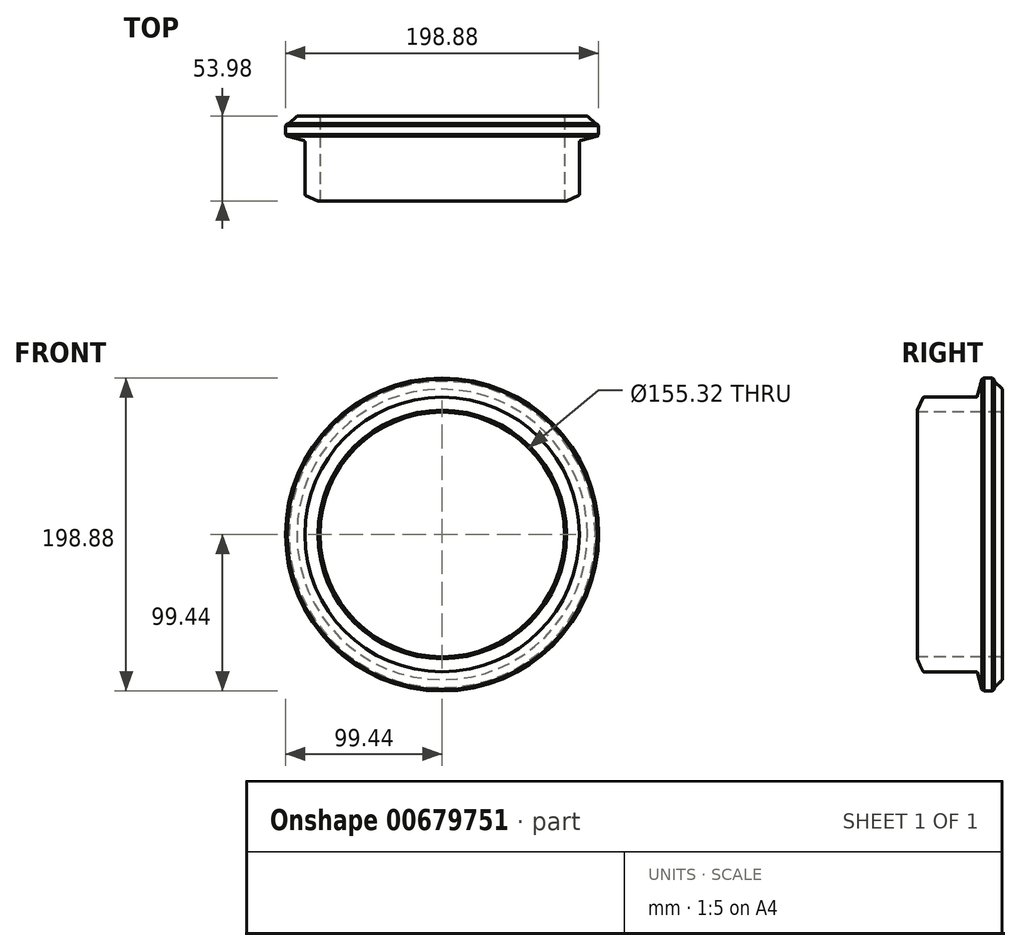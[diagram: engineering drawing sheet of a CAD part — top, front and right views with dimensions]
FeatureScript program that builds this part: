
annotation { "Feature Type Name" : "Feature", "Feature Type Description" : "" }
export const myFeature = defineFeature(function(context is Context, id is Id, definition is map)
    precondition{}
    {
        {
            var Q0;
            Q0=qCreatedBy(makeId("Right.planeOp"),FACE);
            var sketch = newSketch(context, id + "F0", { "sketchPlane" : qUnion([Q0])});
            skPoint(sketch, "E0", {"position": v(0, 77.66) * mm});
            skLineSegment(sketch, "E1", {"start": v(26.99, 77.66) * mm, "end": v(26.99, 92.27) * mm});
            skLineSegment(sketch, "E2", {"start": v(25.8, 93.46) * mm, "end": v(23.09, 96.16) * mm});
            skLineSegment(sketch, "E3", {"start": v(21.96, 97.3) * mm, "end": v(21.96, 99.44) * mm});
            skLineSegment(sketch, "E4", {"start": v(21.96, 99.44) * mm, "end": v(14.27, 99.44) * mm});
            skLineSegment(sketch, "E5", {"start": v(14.27, 99.44) * mm, "end": v(10.99, 87.19) * mm});
            skLineSegment(sketch, "E6", {"start": v(10.99, 87.19) * mm, "end": v(-23.29, 87.19) * mm});
            skLineSegment(sketch, "E7", {"start": v(-23.29, 87.19) * mm, "end": v(-26.99, 78.93) * mm});
            skLineSegment(sketch, "E8", {"start": v(-26.99, 78.42) * mm, "end": v(-26.99, 78.39) * mm});
            skPoint(sketch, "E9.visualSharp", {"position": v(26.99, 77.66) * mm});
            skPoint(sketch, "E10.visualSharp", {"position": v(-26.99, 77.66) * mm});
            skPoint(sketch, "E11.visualSharp", {"position": v(10.99, 87.19) * mm});
            skPoint(sketch, "E12.visualSharp", {"position": v(-26.99, 78.93) * mm});
            skPoint(sketch, "E13.visualSharp", {"position": v(21.96, 97.3) * mm});
            skPoint(sketch, "E14.visualSharp", {"position": v(26.99, 92.27) * mm});
            skLineSegment(sketch, "E15", {"start": v(-61.18, -80.92) * mm, "end": v(40.68, -80.92) * mm, "construction": true});
            skLineSegment(sketch, "E16", {"start": v(21.96, 97.3) * mm, "end": v(26.99, 92.27) * mm});
            skLineSegment(sketch, "E17", {"start": v(26.99, 77.66) * mm, "end": v(-26.99, 77.66) * mm});
            skLineSegment(sketch, "E18", {"start": v(-26.99, 78.93) * mm, "end": v(-26.99, 77.66) * mm});
            skLineSegment(sketch, "E19", {"start": v(-31.2, 0) * mm, "end": v(25.51, 0) * mm, "construction": true});
            skSolve(sketch);
        }
        {
            var Q0;
            {var subQ1=sQuery(id+"F0.wireOp",EDGE,"E1");Q0=makeQuery(id+"F0.imprint","IMPRINT",FACE,{"disambiguationData":[TD([[makeQuery(id+"F0.imprint","IMPRINT",EDGE,{"derivedFrom":subQ1}),1.0]])]});}
            var Q1;
            Q1=sQuery(id+"F0.wireOp",EDGE,"E19");
            revolve(context, id + "F1", {"entities" : qUnion([Q0]), "axis" : qUnion([Q1]), "revolveType" : RevolveType.FULL});
        }
        {
            var Q0;
            Q0=makeQuery(id+"F1.opRevolve","SWEPT_EDGE",EDGE,{"disambiguationData":[OSD([sQuery(id+"F0.wireOp",EDGE,"E5"),sQuery(id+"F0.wireOp",EDGE,"E6")])]});
            var Q1;
            Q1=makeQuery(id+"F1.opRevolve","SWEPT_EDGE",EDGE,{"disambiguationData":[OSD([sQuery(id+"F0.wireOp",EDGE,"E6"),sQuery(id+"F0.wireOp",EDGE,"E7")])]});
            fillet(context, id + "F2", {"entities" : qUnion([Q0, Q1]), "radius" : 0.76 * mm, "tangentPropagation" : true, "allowEdgeOverflow" : false});
        }
        {
            var Q0;
            Q0=makeQuery(id+"F1.opRevolve","SWEPT_EDGE",EDGE,{"disambiguationData":[OSD([sQuery(id+"F0.wireOp",EDGE,"E3"),sQuery(id+"F0.wireOp",EDGE,"E4")])]});
            var Q1;
            Q1=makeQuery(id+"F1.opRevolve","SWEPT_EDGE",EDGE,{"disambiguationData":[OSD([sQuery(id+"F0.wireOp",EDGE,"E4"),sQuery(id+"F0.wireOp",EDGE,"E5")])]});
            chamfer(context, id + "F3", {"entities" : qUnion([Q0, Q1]), "width" : 1.27 * mm, "tangentPropagation" : true});
        }
        {
            var Q0;
            Q0=makeQuery(id+"F1.opRevolve","SWEPT_EDGE",EDGE,{"disambiguationData":[OSD([sQuery(id+"F0.wireOp",EDGE,"E1"),sQuery(id+"F0.wireOp",EDGE,"E17")])]});
            var Q1;
            Q1=makeQuery(id+"F1.opRevolve","SWEPT_EDGE",EDGE,{"disambiguationData":[OSD([sQuery(id+"F0.wireOp",EDGE,"E17"),sQuery(id+"F0.wireOp",EDGE,"E18")])]});
            fillet(context, id + "F4", {"entities" : qUnion([Q0, Q1]), "radius" : 1.27 * mm, "tangentPropagation" : true, "allowEdgeOverflow" : false});
        }
    });
